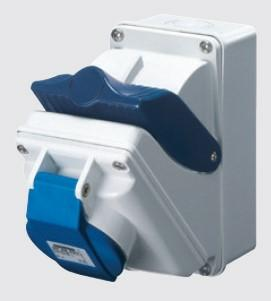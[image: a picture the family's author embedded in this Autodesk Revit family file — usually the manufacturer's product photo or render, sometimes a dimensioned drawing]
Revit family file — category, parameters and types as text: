
# Revit family: Building-IEC309Connections-GEWISS-COMBIBLOC-INTERLOCKED-SOCKET-OUTLETS_IP44
name_source: partatom
category: Apparecchi elettrici
units: mm (PartAtom-declared; Revit-internal decimal feet)

## family parameters
Condiviso = No
Host = Superficie
Mantenere orientamento annotazione = Sì
Punto di calcolo locali = Sì
Quota connettore circolare = Usa diametro
Taglio con vuoti quando caricato = No
Tipo di parte = Normale

## types (18) — shared parameters
BLOCCO = B=C
Catalogue = BUILDING
Electrocod = 2220
FORMULA = 1000 mm  [stored 3.28084 ft]
Frequency = 50/60 Hz
Glow wire test: = 850 °C (active parts) - 650 °C (passive parts)
IDF = 84bc4959-b64c-441e-bbe7-8f1f00ec2266
IDT = 5f0ae1981d6d44abab9cf411e87918d1
IP degree = IP44
Immagine tipo = COMBIBLOC44Fondo.jpg
L = 155 mm
N.poli = 1
Operating temperature: = -25 +40 °C
POMELLO = bianco
PRESA = Giallo
Produttore = GEWISS S.p.A.
Prospetto di default = 1219 mm
Protection = NO (SBF)
SEO = Interlocked outlet
STRUTTURA = RAL - 7035
STRUTTURA ALTA = blue
Shock resistance = IK08
Spostamento_S = 1500 mm
Technical sheet = https://www.gewiss.com
Thermo-pressure with ball = 125 °C (active parts) - 80 °C (passive parts)
Typology = Compact
URL = https://www.gewiss.com
VETRO = Vetro
Version file RFA = 21.4
Voltaggio = 0 V
W = 115 mm
With back-mounting box = Yes

## per-type parameters (varying)
| type | Colour: | Descrizione | Modello | No. of poles | Rated current (A) | Rated voltage | Reference h |
| GW66414 - COMBIBLOC W.B.IP44 3P+N+E 32A 110V 4H | Yellow | COMBIBLOC W.B.IP44 3P+N+E 32A 110V 4H | GW66414 | 3P+N+E | 32 | 100-130V | 4 |
| GW66418 - COMBIBLOC W.B.IP44 2P+E 32A 400V 9H | Red | COMBIBLOC W.B.IP44 2P+E 32A 400V 9H | GW66418 | 2P+E | 32 | 380-415V | 9 |
| GW66403 - COMBIBLOC W.B.IP44 3P+N+E 16A 110V 4H | Yellow | COMBIBLOC W.B.IP44 3P+N+E 16A 110V 4H | GW66403 | 3P+N+E | 16 | 100-130V | 4 |
| GW66408 - COMBIBLOC W.B.IP44 3P+E 16A 400V 6H | Red | COMBIBLOC W.B.IP44 3P+E 16A 400V 6H | GW66408 | 3P+E | 16 | 380-415V | 6 |
| GW66413 - COMBIBLOC W.B.IP44 3P+E 32A 110V 4H | Yellow | COMBIBLOC W.B.IP44 3P+E 32A 110V 4H | GW66413 | 3P+E | 32 | 100-130V | 4 |
| GW66406 - COMBIBLOC W.B.IP44 3P+N+E 16A 230V 9H | Blue | COMBIBLOC W.B.IP44 3P+N+E 16A 230V 9H | GW66406 | 3P+N+E | 16 | 200-250V | 9 |
| GW66415 - COMBIBLOC W.B.IP44 2P+E 32A 230V 6H | Blue | COMBIBLOC W.B.IP44 2P+E 32A 230V 6H | GW66415 | 2P+E | 32 | 200-250V | 6 |
| GW66419 - COMBIBLOC W.B.IP44 3P+E 32A 400V 6H | Red | COMBIBLOC W.B.IP44 3P+E 32A 400V 6H | GW66419 | 3P+E | 32 | 380-415V | 6 |
| GW66404 - COMBIBLOC W.B.IP44 2P+E 16A 230V 6H | Blue | COMBIBLOC W.B.IP44 2P+E 16A 230V 6H | GW66404 | 2P+E | 16 | 200-250V | 6 |
| GW66401 - COMBIBLOC W.B.IP44 2P+E 16A 110V 4H | Yellow | COMBIBLOC W.B.IP44 2P+E 16A 110V 4H | GW66401 | 2P+E | 16 | 100-130V | 4 |
| GW66407 - COMBIBLOC W.B.IP44 2P+E 16A 400V 9H | Red | COMBIBLOC W.B.IP44 2P+E 16A 400V 9H | GW66407 | 2P+E | 16 | 380-415V | 9 |
| GW66409 - COMBIBLOC W.B.IP44 3P+N+E 16A 400V 6H | Red | COMBIBLOC W.B.IP44 3P+N+E 16A 400V 6H | GW66409 | 3P+N+E | 16 | 380-415V | 6 |
| GW66402 - COMBIBLOC W.B.IP44 3P+E 16A 110V 4H | Yellow | COMBIBLOC W.B.IP44 3P+E 16A 110V 4H | GW66402 | 3P+E | 16 | 100-130V | 4 |
| GW66416 - COMBIBLOC W.B.IP44 3P+E 32A 230V 9H | Blue | COMBIBLOC W.B.IP44 3P+E 32A 230V 9H | GW66416 | 3P+E | 32 | 200-250V | 9 |
| GW66420 - COMBIBLOC W.B.IP44 3P+N+E 32A 400V 6H | Red | COMBIBLOC W.B.IP44 3P+N+E 32A 400V 6H | GW66420 | 3P+N+E | 32 | 380-415V | 6 |
| GW66412 - COMBIBLOC W.B.IP44 2P+E 32A 110V4H | Yellow | COMBIBLOC W.B.IP44 2P+E 32A 110V4H | GW66412 | 2P+E | 32 | 100-130V | 4 |
| GW66417 - COMBIBLOC W.B.IP44 3P+N+E 32A 230V 9H | Blue | COMBIBLOC W.B.IP44 3P+N+E 32A 230V 9H | GW66417 | 3P+N+E | 32 | 200-250V | 9 |
| GW66405 - COMBIBLOC W.B.IP44 3P+E 16A 230V 9H | Blue | COMBIBLOC W.B.IP44 3P+E 16A 230V 9H | GW66405 | 3P+E | 16 | 200-250V | 9 |

note: [stored X ft] marks values corroborated as IEEE doubles in the binary element streams (Revit-internal decimal feet)

## geometry (parser evidence)
native form markers: Sweep x4
no freeform markers — native parametric forms only
